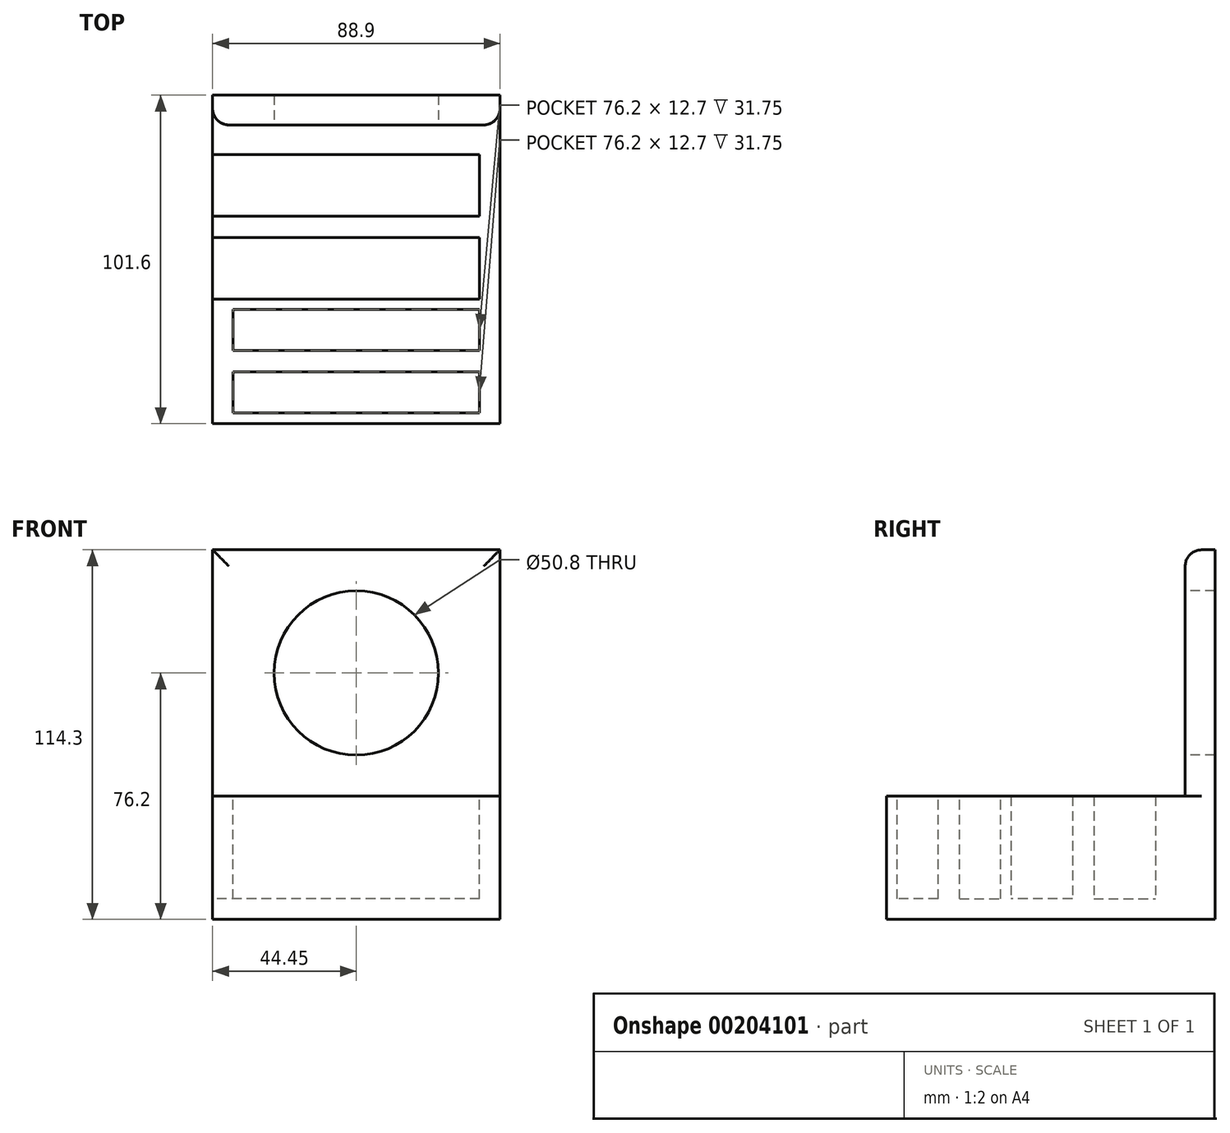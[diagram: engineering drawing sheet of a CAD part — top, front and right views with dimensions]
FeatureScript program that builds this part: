
annotation { "Feature Type Name" : "Feature", "Feature Type Description" : "" }
export const myFeature = defineFeature(function(context is Context, id is Id, definition is map)
    precondition{}
    {
        {
            var Q0;
            Q0=qCreatedBy(makeId("Front.planeOp"),FACE);
            var sketch = newSketch(context, id + "F0", { "sketchPlane" : qUnion([Q0])});
            skLineSegment(sketch, "E0", {"start": v(0, 19.05) * mm, "end": v(-44.45, 19.05) * mm});
            skLineSegment(sketch, "E1", {"start": v(-44.45, 19.05) * mm, "end": v(-44.45, 0) * mm});
            skLineSegment(sketch, "E2.MirrorCS", {"start": v(44.45, 19.05) * mm, "end": v(44.45, 0) * mm});
            skLineSegment(sketch, "E3.MirrorCS", {"start": v(0, 19.05) * mm, "end": v(44.45, 19.05) * mm});
            skLineSegment(sketch, "E4.MirrorCS", {"start": v(-44.45, -19.05) * mm, "end": v(-44.45, 0) * mm});
            skLineSegment(sketch, "E5.MirrorCS", {"start": v(0, -19.05) * mm, "end": v(-44.45, -19.05) * mm});
            skLineSegment(sketch, "E6.MirrorCS", {"start": v(0, -19.05) * mm, "end": v(44.45, -19.05) * mm});
            skLineSegment(sketch, "E7.MirrorCS", {"start": v(44.45, -19.05) * mm, "end": v(44.45, 0) * mm});
            skSolve(sketch);
        }
        {
            var Q0;
            Q0=qSketchRegion(id+"F0",true);
            extrude(context, id + "F1", {"entities" : qUnion([Q0]), "depth" : 101.6 * mm});
        }
        {
            var Q0;
            Q0=makeQuery(id+"F1.opExtrude","SWEPT_FACE",FACE,{"disambiguationData":[OSD([sQuery(id+"F0.wireOp",EDGE,"E0"),sQuery(id+"F0.wireOp",EDGE,"E3.MirrorCS")])]});
            var sketch = newSketch(context, id + "F2", { "sketchPlane" : qUnion([Q0])});
            skLineSegment(sketch, "E8", {"start": v(0, 0) * mm, "end": v(0, -101.6) * mm, "construction": true});
            skLineSegment(sketch, "E9", {"start": v(0, -85.6) * mm, "end": v(-38.1, -85.6) * mm});
            skLineSegment(sketch, "E10", {"start": v(-38.1, -85.6) * mm, "end": v(-38.1, -98.3) * mm});
            skLineSegment(sketch, "E11", {"start": v(-38.1, -98.3) * mm, "end": v(0, -98.3) * mm});
            skLineSegment(sketch, "E12.MirrorCS", {"start": v(0, -85.6) * mm, "end": v(38.1, -85.6) * mm});
            skLineSegment(sketch, "E13.MirrorCS", {"start": v(38.1, -85.6) * mm, "end": v(38.1, -98.3) * mm});
            skLineSegment(sketch, "E14.MirrorCS", {"start": v(38.1, -98.3) * mm, "end": v(0, -98.3) * mm});
            skLineSegment(sketch, "E15", {"start": v(-44.45, -82.3) * mm, "end": v(44.45, -82.3) * mm, "construction": true});
            skLineSegment(sketch, "E16.MirrorCS", {"start": v(0, -79) * mm, "end": v(-38.1, -79) * mm});
            skLineSegment(sketch, "E17.MirrorCS", {"start": v(0, -79) * mm, "end": v(38.1, -79) * mm});
            skLineSegment(sketch, "E18.MirrorCS", {"start": v(38.1, -79) * mm, "end": v(38.1, -66.3) * mm});
            skLineSegment(sketch, "E19.MirrorCS", {"start": v(38.1, -66.3) * mm, "end": v(0, -66.3) * mm});
            skLineSegment(sketch, "E20.MirrorCS", {"start": v(-38.1, -66.3) * mm, "end": v(0, -66.3) * mm});
            skLineSegment(sketch, "E21.MirrorCS", {"start": v(-38.1, -79) * mm, "end": v(-38.1, -66.3) * mm});
            skSolve(sketch);
        }
        {
            var Q0;
            Q0=qSketchRegion(id+"F2",true);
            extrude(context, id + "F3", {"entities" : qUnion([Q0]), "operationType" : NewBodyOperationType.REMOVE, "oppositeDirection" : true, "depth" : 31.75 * mm});
        }
        {
            var Q0;
            Q0=makeQuery(id+"F1.opExtrude","SWEPT_FACE",FACE,{"disambiguationData":[OSD([sQuery(id+"F0.wireOp",EDGE,"E1"),sQuery(id+"F0.wireOp",EDGE,"E4.MirrorCS")])]});
            var sketch = newSketch(context, id + "F4", { "sketchPlane" : qUnion([Q0])});
            skLineSegment(sketch, "E22.0.0", {"start": v(79, 19.05) * mm, "end": v(66.3, 19.05) * mm, "construction": true});
            skLineSegment(sketch, "E22.0.1", {"start": v(66.3, 19.05) * mm, "end": v(66.3, -12.7) * mm, "construction": true});
            skLineSegment(sketch, "E22.0.2", {"start": v(66.3, -12.7) * mm, "end": v(79, -12.7) * mm, "construction": true});
            skLineSegment(sketch, "E22.0.3", {"start": v(79, -12.7) * mm, "end": v(79, 19.05) * mm, "construction": true});
            skLineSegment(sketch, "E23.bottom", {"start": v(44.07, 19.05) * mm, "end": v(63.12, 19.05) * mm});
            skLineSegment(sketch, "E23.top", {"start": v(44.07, -12.7) * mm, "end": v(63.12, -12.7) * mm});
            skLineSegment(sketch, "E23.left", {"start": v(44.07, 19.05) * mm, "end": v(44.07, -12.7) * mm});
            skLineSegment(sketch, "E23.right", {"start": v(63.12, 19.05) * mm, "end": v(63.12, -12.7) * mm});
            skLineSegment(sketch, "E24", {"start": v(40.77, 19.05) * mm, "end": v(40.77, -19.05) * mm, "construction": true});
            skLineSegment(sketch, "E25.MirrorCS", {"start": v(37.47, 19.05) * mm, "end": v(18.42, 19.05) * mm});
            skLineSegment(sketch, "E26.MirrorCS", {"start": v(37.47, 19.05) * mm, "end": v(37.47, -12.7) * mm});
            skLineSegment(sketch, "E27.MirrorCS", {"start": v(37.47, -12.7) * mm, "end": v(18.42, -12.7) * mm});
            skLineSegment(sketch, "E28.MirrorCS", {"start": v(18.42, 19.05) * mm, "end": v(18.42, -12.7) * mm});
            skSolve(sketch);
        }
        {
            var Q0;
            Q0=qSketchRegion(id+"F4",true);
            extrude(context, id + "F5", {"entities" : qUnion([Q0]), "operationType" : NewBodyOperationType.REMOVE, "endBound" : BoundingType.THROUGH_ALL, "oppositeDirection" : true, "depth" : 25.4 * mm});
        }
        {
            var Q0;
            {var subQ2=sQuery(id+"F0.wireOp",EDGE,"E3.MirrorCS");var subQ5=sQuery(id+"F0.wireOp",EDGE,"E0");Q0=makeQuery(id+"F5.boolean.opBoolean","SPLIT",FACE,{"disambiguationData":[TD([makeQuery(id+"F5.opExtrude","SWEPT_FACE",FACE,{"disambiguationData":[OSD([sQuery(id+"F4.wireOp",EDGE,"E28.MirrorCS")])]})])],"derivedFrom":makeQuery(id+"F1.opExtrude","SWEPT_FACE",FACE,{"disambiguationData":[OSD([subQ5,subQ2])]})});}
            var sketch = newSketch(context, id + "F6", { "sketchPlane" : qUnion([Q0])});
            skLineSegment(sketch, "E29.bottom", {"start": v(-44.45, 0) * mm, "end": v(44.45, 0) * mm});
            skLineSegment(sketch, "E29.top", {"start": v(-44.45, -9.2) * mm, "end": v(44.45, -9.2) * mm});
            skLineSegment(sketch, "E29.left", {"start": v(-44.45, 0) * mm, "end": v(-44.45, -9.2) * mm});
            skLineSegment(sketch, "E29.right", {"start": v(44.45, 0) * mm, "end": v(44.45, -9.2) * mm});
            skSolve(sketch);
        }
        {
            var Q0;
            Q0=qSketchRegion(id+"F6",true);
            extrude(context, id + "F7", {"entities" : qUnion([Q0]), "operationType" : NewBodyOperationType.ADD, "depth" : 76.2 * mm});
        }
        {
            var Q0;
            Q0=makeQuery(id+"F7.opExtrude","SWEPT_FACE",FACE,{"disambiguationData":[OSD([sQuery(id+"F6.wireOp",EDGE,"E29.top")])]});
            var sketch = newSketch(context, id + "F8", { "sketchPlane" : qUnion([Q0])});
            skCircle(sketch, "E30", {"center": v(0, 57.15) * mm, "radius": 25.4 * mm});
            skPoint(sketch, "E30.centerSnap0", {"position": v(-44.45, 57.15) * mm});
            skSolve(sketch);
        }
        {
            var Q0;
            Q0=qSketchRegion(id+"F8",true);
            extrude(context, id + "F9", {"entities" : qUnion([Q0]), "operationType" : NewBodyOperationType.REMOVE, "endBound" : BoundingType.THROUGH_ALL, "oppositeDirection" : true, "depth" : 25.4 * mm});
        }
        {
            var Q0;
            Q0=makeQuery(id+"F7.opExtrude","CAP_EDGE",EDGE,{"disambiguationData":[OSD([sQuery(id+"F6.wireOp",EDGE,"E29.top")])],"isStart":false});
            var Q1;
            Q1=makeQuery(id+"F7.opExtrude","SWEPT_EDGE",EDGE,{"disambiguationData":[OSD([sQuery(id+"F0.wireOp",EDGE,"E0"),sQuery(id+"F0.wireOp",EDGE,"E1"),sQuery(id+"F6.wireOp",EDGE,"E29.top"),sQuery(id+"F6.wireOp",EDGE,"E29.left")])]});
            var Q2;
            Q2=makeQuery(id+"F7.opExtrude","SWEPT_EDGE",EDGE,{"disambiguationData":[OSD([sQuery(id+"F0.wireOp",EDGE,"E2.MirrorCS"),sQuery(id+"F0.wireOp",EDGE,"E3.MirrorCS"),sQuery(id+"F6.wireOp",EDGE,"E29.top"),sQuery(id+"F6.wireOp",EDGE,"E29.right")])]});
            var Q3;
            Q3=makeQuery(id+"F9.boolean.opBoolean","COPY",EDGE,{"derivedFrom":makeQuery(id+"F9.opExtrude","CAP_EDGE",EDGE,{"disambiguationData":[OSD([sQuery(id+"F8.wireOp",EDGE,"E30")])],"isStart":true})});
            fillet(context, id + "F10", {"entities" : qUnion([Q0, Q1, Q2, Q3]), "radius" : 5.08 * mm, "tangentPropagation" : true, "allowEdgeOverflow" : false});
        }
        {
            var Q0;
            Q0=makeQuery(id+"F7.boolean.opBoolean","MERGE",FACE,{"derivedFrom":[makeQuery(id+"F1.opExtrude","SWEPT_FACE",FACE,{"disambiguationData":[OSD([sQuery(id+"F0.wireOp",EDGE,"E2.MirrorCS"),sQuery(id+"F0.wireOp",EDGE,"E7.MirrorCS")])]}),makeQuery(id+"F7.opExtrude","SWEPT_FACE",FACE,{"disambiguationData":[OSD([sQuery(id+"F6.wireOp",EDGE,"E29.right")])]})]});
            var sketch = newSketch(context, id + "F11", { "sketchPlane" : qUnion([Q0])});
            skLineSegment(sketch, "E31.bottom", {"start": v(-63.12, 19.05) * mm, "end": v(-44.07, 19.05) * mm});
            skLineSegment(sketch, "E31.top", {"start": v(-63.12, -12.7) * mm, "end": v(-44.07, -12.7) * mm});
            skLineSegment(sketch, "E31.left", {"start": v(-63.12, 19.05) * mm, "end": v(-63.12, -12.7) * mm});
            skLineSegment(sketch, "E31.right", {"start": v(-44.07, 19.05) * mm, "end": v(-44.07, -12.7) * mm});
            skLineSegment(sketch, "E32.bottom", {"start": v(-37.47, 19.05) * mm, "end": v(-18.42, 19.05) * mm});
            skLineSegment(sketch, "E32.top", {"start": v(-37.47, -12.7) * mm, "end": v(-18.42, -12.7) * mm});
            skLineSegment(sketch, "E32.left", {"start": v(-37.47, 19.05) * mm, "end": v(-37.47, -12.7) * mm});
            skLineSegment(sketch, "E32.right", {"start": v(-18.42, 19.05) * mm, "end": v(-18.42, -12.7) * mm});
            skSolve(sketch);
        }
        {
            var Q0;
            Q0 = qSketchRegion(id + "F11", true);
            var Q1;
            Q1=makeQuery(id+"F3.boolean.opBoolean","COPY",FACE,{"derivedFrom":makeQuery(id+"F3.opExtrude","SWEPT_FACE",FACE,{"disambiguationData":[OSD([sQuery(id+"F2.wireOp",EDGE,"E18.MirrorCS")])]})});
            extrude(context, id + "F12", {"entities" : qUnion([Q0]), "operationType" : NewBodyOperationType.ADD, "endBound" : BoundingType.UP_TO_SURFACE, "oppositeDirection" : true, "endBoundEntityFace" : qUnion([Q1]), "depth" : 25.4 * mm});
        }
    });
